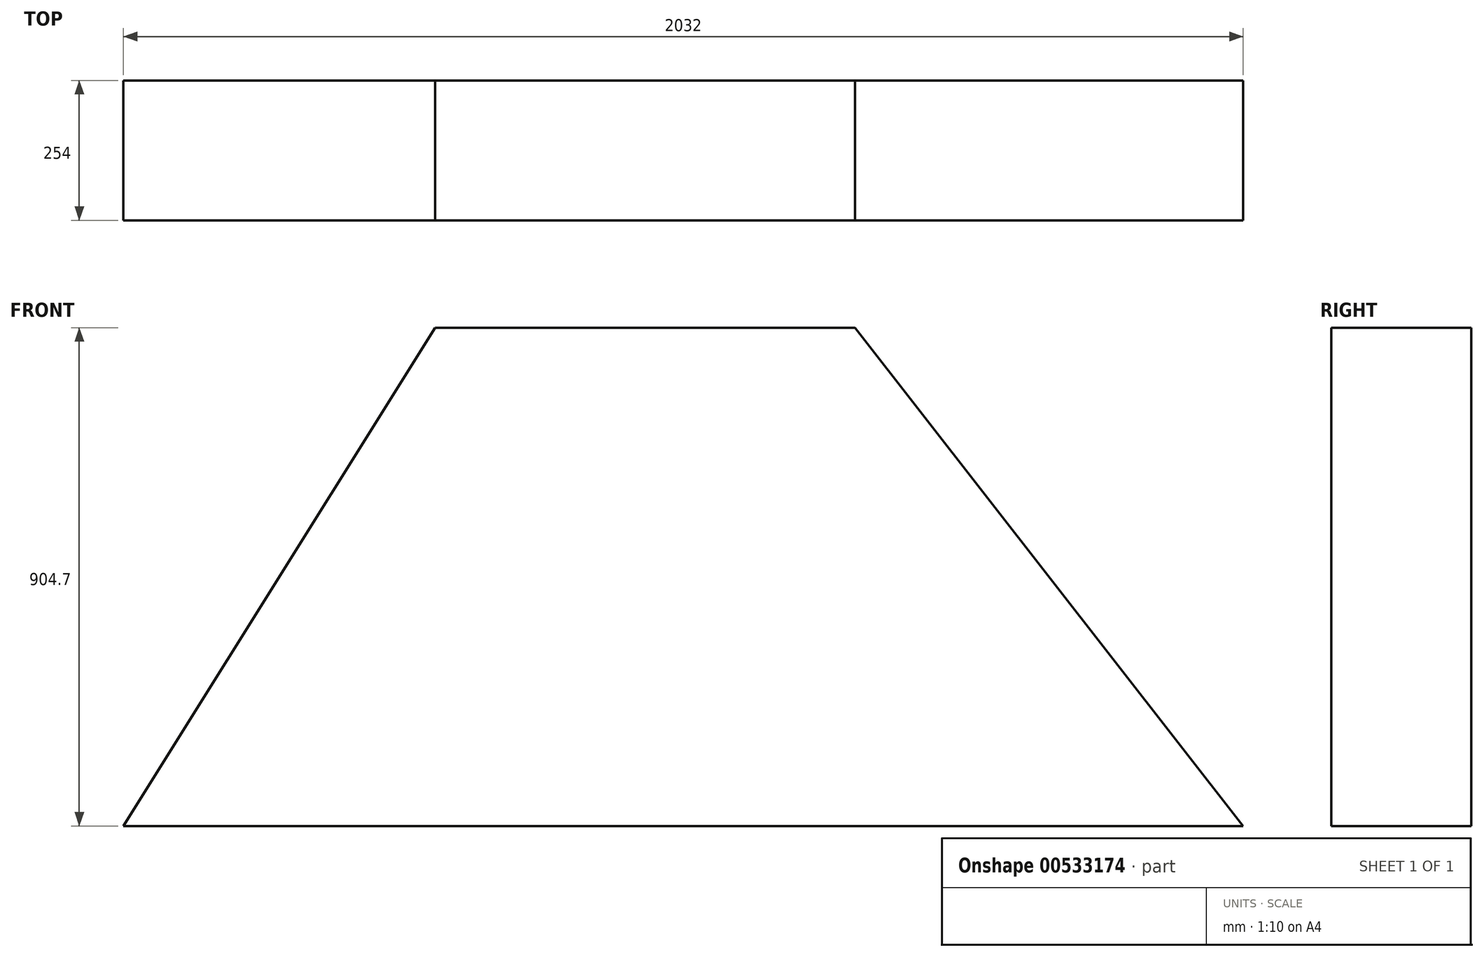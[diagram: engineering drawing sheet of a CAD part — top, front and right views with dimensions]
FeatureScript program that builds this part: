
annotation { "Feature Type Name" : "Feature", "Feature Type Description" : "" }
export const myFeature = defineFeature(function(context is Context, id is Id, definition is map)
    precondition{}
    {
        {
            var Q0;
            Q0=qCreatedBy(makeId("Front.planeOp"),FACE);
            var sketch = newSketch(context, id + "F0", { "sketchPlane" : qUnion([Q0])});
            skLineSegment(sketch, "E0", {"start": v(0, 0) * mm, "end": v(762, 0) * mm});
            skLineSegment(sketch, "E1", {"start": v(0, 0) * mm, "end": v(-565.32, -904.7) * mm});
            skLineSegment(sketch, "E2", {"start": v(-565.32, -904.7) * mm, "end": v(1466.68, -904.7) * mm});
            skLineSegment(sketch, "E3", {"start": v(1466.68, -904.7) * mm, "end": v(762, 0) * mm});
            skSolve(sketch);
        }
        {
            var Q0;
            Q0=makeQuery(id+"F0.imprint","IMPRINT",FACE,{"disambiguationData":[TD([[makeQuery(id+"F0.imprint","IMPRINT",EDGE,{"derivedFrom":sQuery(id+"F0.wireOp",EDGE,"E0")}),-1.0]])]});
            extrude(context, id + "F1", {"entities" : qUnion([Q0]), "depth" : 254 * mm, "offsetDistance" : 25.4 * mm});
        }
    });
